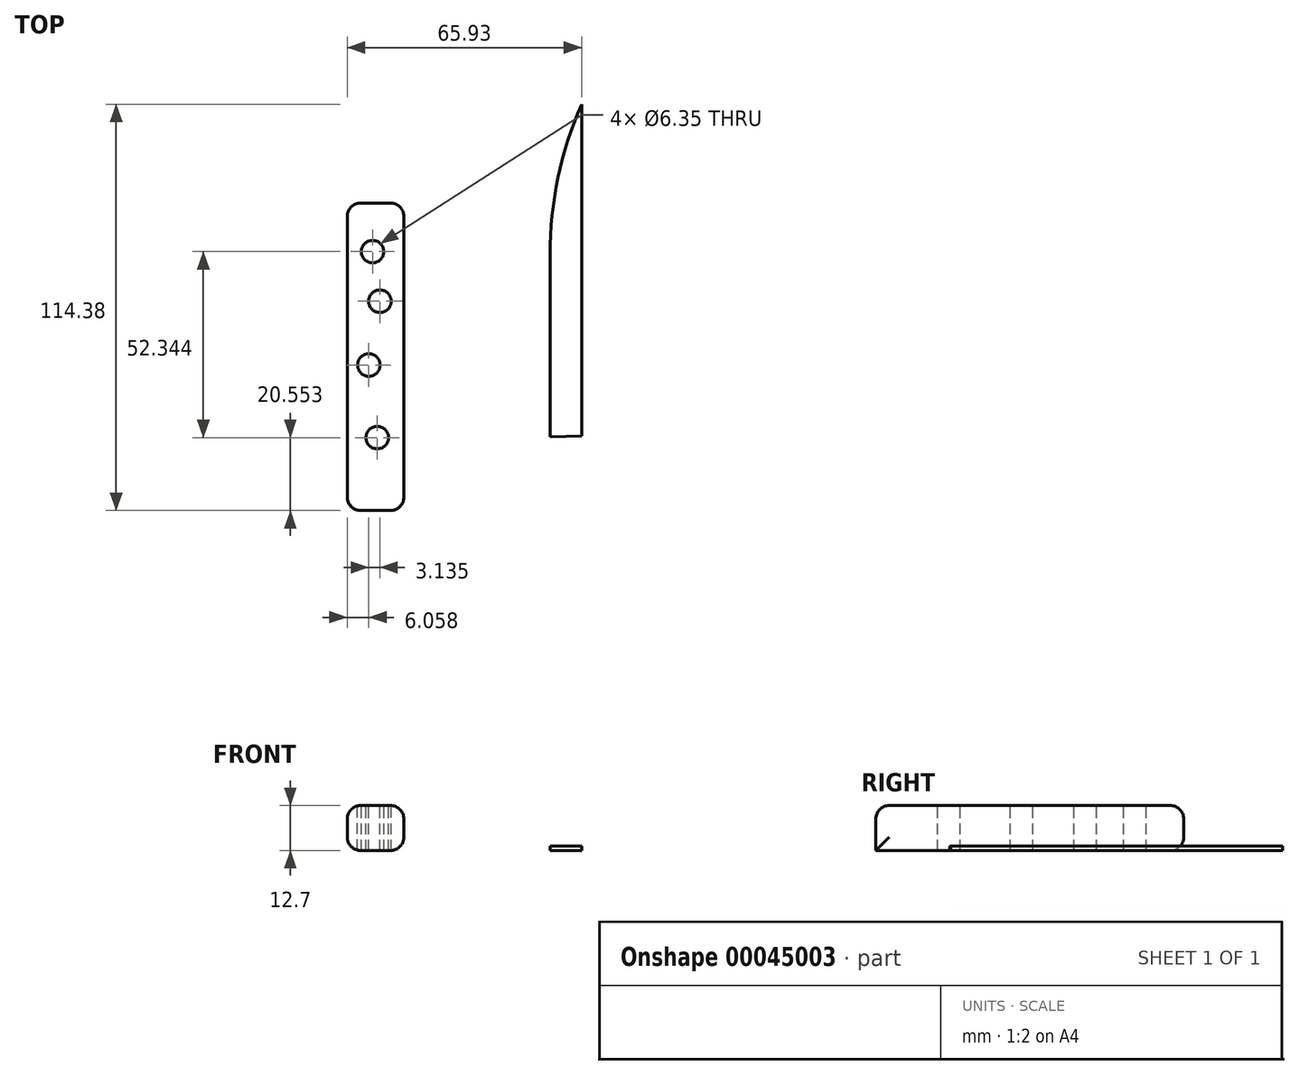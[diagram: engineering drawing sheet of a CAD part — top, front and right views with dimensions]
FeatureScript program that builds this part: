
annotation { "Feature Type Name" : "Feature", "Feature Type Description" : "" }
export const myFeature = defineFeature(function(context is Context, id is Id, definition is map)
    precondition{}
    {
        {
            var Q0;
            Q0=qCreatedBy(makeId("Top.planeOp"),FACE);
            var sketch = newSketch(context, id + "F0", { "sketchPlane" : qUnion([Q0])});
            skLineSegment(sketch, "E0", {"start": v(0, -43.15) * mm, "end": v(0, 8.19) * mm});
            skArc(sketch, "E1", {"start": v(0, 8.19) * mm, "mid": v(2.25, 29.78) * mm, "end": v(8.9, 50.45) * mm});
            skLineSegment(sketch, "E2", {"start": v(8.9, 50.45) * mm, "end": v(8.9, -42.9) * mm});
            skLineSegment(sketch, "E3", {"start": v(0, -43.15) * mm, "end": v(8.9, -42.9) * mm});
            skSolve(sketch);
        }
        {
            var Q0;
            Q0=makeQuery(id+"F0.imprint","IMPRINT",FACE,{"disambiguationData":[TD([[makeQuery(id+"F0.imprint","IMPRINT",EDGE,{"derivedFrom":sQuery(id+"F0.wireOp",EDGE,"E0")}),-1.0]])]});
            extrude(context, id + "F1", {"entities" : qUnion([Q0]), "depth" : 1.27 * mm});
        }
        {
            var Q0;
            Q0=qCreatedBy(makeId("Top.planeOp"),FACE);
            var sketch = newSketch(context, id + "F2", { "sketchPlane" : qUnion([Q0])});
            skLineSegment(sketch, "E4.bottom", {"start": v(-57.04, 22.68) * mm, "end": v(-41.12, 22.68) * mm});
            skLineSegment(sketch, "E4.top", {"start": v(-57.04, -63.93) * mm, "end": v(-41.12, -63.93) * mm});
            skLineSegment(sketch, "E4.left", {"start": v(-57.04, 22.68) * mm, "end": v(-57.04, -63.93) * mm});
            skLineSegment(sketch, "E4.right", {"start": v(-41.12, 22.68) * mm, "end": v(-41.12, -63.93) * mm});
            skSolve(sketch);
        }
        {
            var Q0;
            Q0=makeQuery(id+"F2.imprint","IMPRINT",FACE,{"disambiguationData":[TD([[makeQuery(id+"F2.imprint","IMPRINT",EDGE,{"derivedFrom":sQuery(id+"F2.wireOp",EDGE,"E4.bottom")}),-1.0]])]});
            extrude(context, id + "F3", {"entities" : qUnion([Q0]), "depth" : 12.7 * mm});
        }
        {
            var Q0;
            Q0=makeQuery(id+"F3.opExtrude","CAP_EDGE",EDGE,{"disambiguationData":[OSD([sQuery(id+"F2.wireOp",EDGE,"E4.left")])],"isStart":false});
            var Q1;
            Q1=makeQuery(id+"F3.opExtrude","CAP_EDGE",EDGE,{"disambiguationData":[OSD([sQuery(id+"F2.wireOp",EDGE,"E4.right")])],"isStart":false});
            var Q2;
            Q2=makeQuery(id+"F3.opExtrude","CAP_FACE",FACE,{"disambiguationData":[OSD([sQuery(id+"F2.wireOp",EDGE,"E4.bottom"),sQuery(id+"F2.wireOp",EDGE,"E4.top"),sQuery(id+"F2.wireOp",EDGE,"E4.left"),sQuery(id+"F2.wireOp",EDGE,"E4.right")])],"isStart":false});
            var Q3;
            Q3=makeQuery(id+"F3.opExtrude","CAP_EDGE",EDGE,{"disambiguationData":[OSD([sQuery(id+"F2.wireOp",EDGE,"E4.top")])],"isStart":false});
            var Q4;
            Q4=makeQuery(id+"F3.opExtrude","CAP_EDGE",EDGE,{"disambiguationData":[OSD([sQuery(id+"F2.wireOp",EDGE,"E4.bottom")])],"isStart":false});
            var Q5;
            Q5=makeQuery(id+"F3.opExtrude","SWEPT_EDGE",EDGE,{"disambiguationData":[OSD([sQuery(id+"F2.wireOp",EDGE,"E4.bottom"),sQuery(id+"F2.wireOp",EDGE,"E4.left")])]});
            var Q6;
            Q6=makeQuery(id+"F3.opExtrude","SWEPT_EDGE",EDGE,{"disambiguationData":[OSD([sQuery(id+"F2.wireOp",EDGE,"E4.bottom"),sQuery(id+"F2.wireOp",EDGE,"E4.right")])]});
            var Q7;
            Q7=makeQuery(id+"F3.opExtrude","CAP_EDGE",EDGE,{"disambiguationData":[OSD([sQuery(id+"F2.wireOp",EDGE,"E4.bottom")])],"isStart":true});
            var Q8;
            Q8=makeQuery(id+"F3.opExtrude","CAP_EDGE",EDGE,{"disambiguationData":[OSD([sQuery(id+"F2.wireOp",EDGE,"E4.left")])],"isStart":true});
            var Q9;
            Q9=makeQuery(id+"F3.opExtrude","CAP_EDGE",EDGE,{"disambiguationData":[OSD([sQuery(id+"F2.wireOp",EDGE,"E4.right")])],"isStart":true});
            var Q10;
            Q10=makeQuery(id+"F3.opExtrude","SWEPT_EDGE",EDGE,{"disambiguationData":[OSD([sQuery(id+"F2.wireOp",EDGE,"E4.top"),sQuery(id+"F2.wireOp",EDGE,"E4.right")])]});
            var Q11;
            Q11=makeQuery(id+"F3.opExtrude","SWEPT_EDGE",EDGE,{"disambiguationData":[OSD([sQuery(id+"F2.wireOp",EDGE,"E4.top"),sQuery(id+"F2.wireOp",EDGE,"E4.left")])]});
            fillet(context, id + "F4", {"entities" : qUnion([Q0, Q1, Q2, Q3, Q4, Q5, Q6, Q7, Q8, Q9, Q10, Q11]), "radius" : 3.8 * mm, "tangentPropagation" : true, "allowEdgeOverflow" : false});
        }
        {
            var Q0;
            Q0=makeQuery(id+"F3.opExtrude","CAP_FACE",FACE,{"disambiguationData":[OSD([sQuery(id+"F2.wireOp",EDGE,"E4.bottom"),sQuery(id+"F2.wireOp",EDGE,"E4.top"),sQuery(id+"F2.wireOp",EDGE,"E4.left"),sQuery(id+"F2.wireOp",EDGE,"E4.right")])],"isStart":false});
            var sketch = newSketch(context, id + "F5", { "sketchPlane" : qUnion([Q0])});
            skCircle(sketch, "E5", {"center": v(-49.94, 8.97) * mm, "radius": 2.5 * mm});
            skCircle(sketch, "E6", {"center": v(-47.85, -5) * mm, "radius": 2.85 * mm});
            skCircle(sketch, "E7", {"center": v(-50.98, -22.95) * mm, "radius": 1.63 * mm});
            skCircle(sketch, "E8", {"center": v(-48.6, -43.38) * mm, "radius": 3.21 * mm});
            skSolve(sketch);
        }
        {
            var Q0;
            Q0=sQuery(id+"F5.wireOp",VERTEX,"E7.center");
            var Q1;
            Q1=sQuery(id+"F5.wireOp",VERTEX,"E5.center");
            var Q2;
            Q2=sQuery(id+"F5.wireOp",VERTEX,"E6.center");
            var Q3;
            Q3=sQuery(id+"F5.wireOp",VERTEX,"E8.center");
            var Q4;
            Q4=makeQuery(id+"F3.opExtrude","SWEPT_BODY",BODY,{"disambiguationData":[OSD([sQuery(id+"F2.wireOp",EDGE,"E4.bottom"),sQuery(id+"F2.wireOp",EDGE,"E4.top"),sQuery(id+"F2.wireOp",EDGE,"E4.left"),sQuery(id+"F2.wireOp",EDGE,"E4.right")])]});
            hole(context, id + "F6", {"style" : HoleStyle.SIMPLE, "holeDiameter" : 6.35 * mm, "endStyle" : HoleEndStyle.THROUGH, "locations" : qUnion([Q0, Q1, Q2, Q3]), "scope" : qUnion([Q4])});
        }
    });
